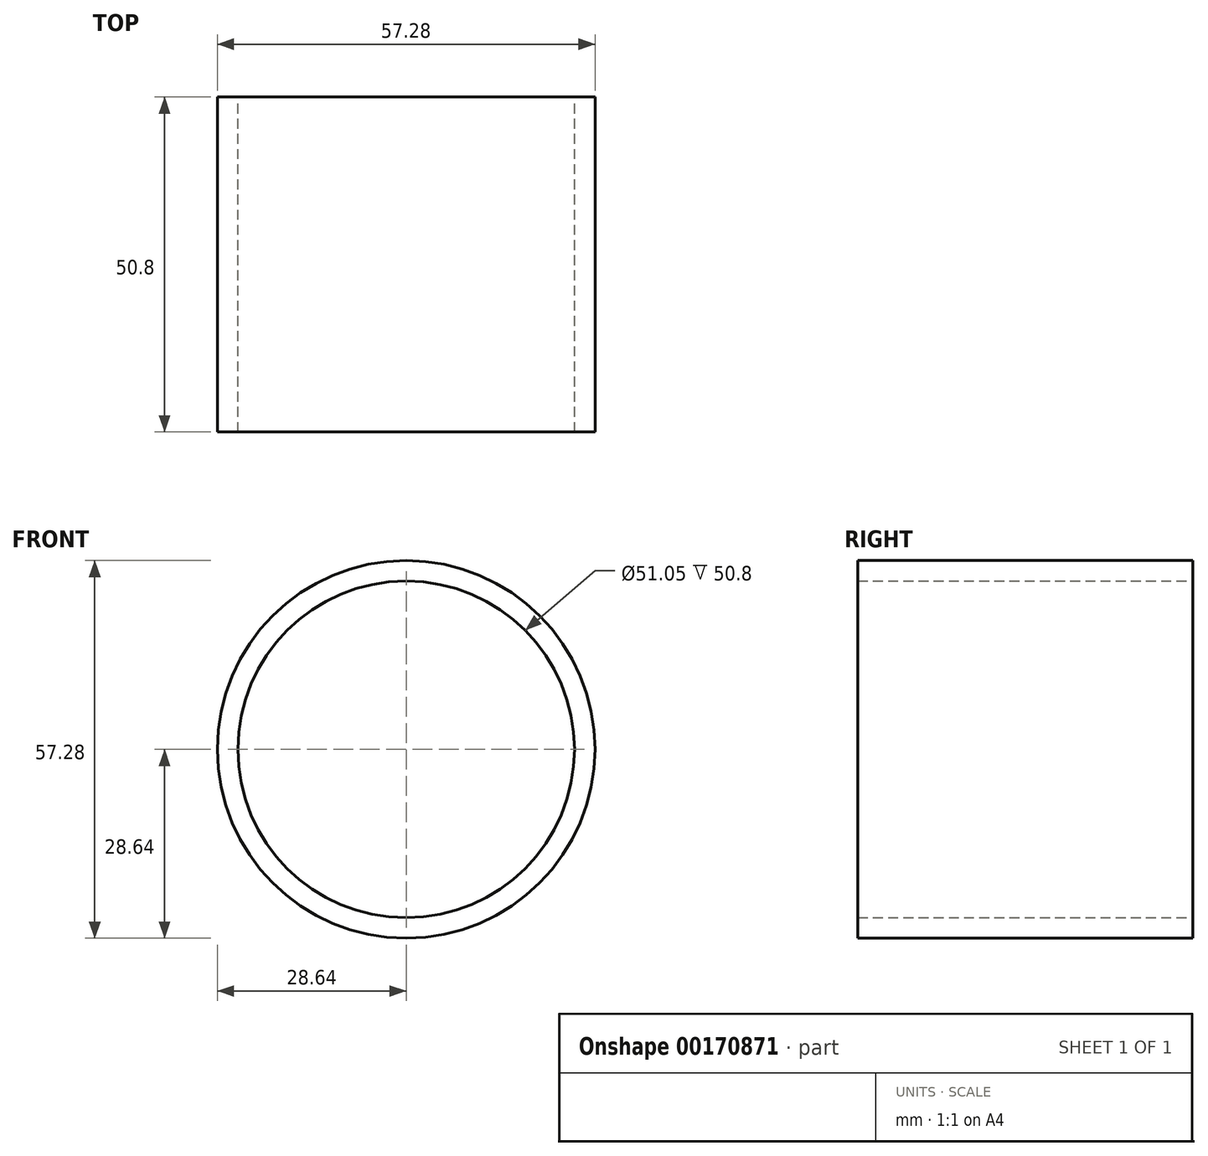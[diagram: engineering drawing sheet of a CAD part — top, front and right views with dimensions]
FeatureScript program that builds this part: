
annotation { "Feature Type Name" : "Feature", "Feature Type Description" : "" }
export const myFeature = defineFeature(function(context is Context, id is Id, definition is map)
    precondition{}
    {
        {
            var Q0;
            Q0=qCreatedBy(makeId("Front.planeOp"),FACE);
            var sketch = newSketch(context, id + "F0", { "sketchPlane" : qUnion([Q0])});
            skCircle(sketch, "E0", {"center": v(0, 0) * mm, "radius": 25.53 * mm});
            skCircle(sketch, "E1", {"center": v(0, 0) * mm, "radius": 28.64 * mm});
            skSolve(sketch);
        }
        {
            var Q0;
            Q0 = qSketchRegion(id + "F0", true);
            extrude(context, id + "F1", {"entities" : qUnion([Q0]), "depth" : 50.8 * mm});
        }
    });
